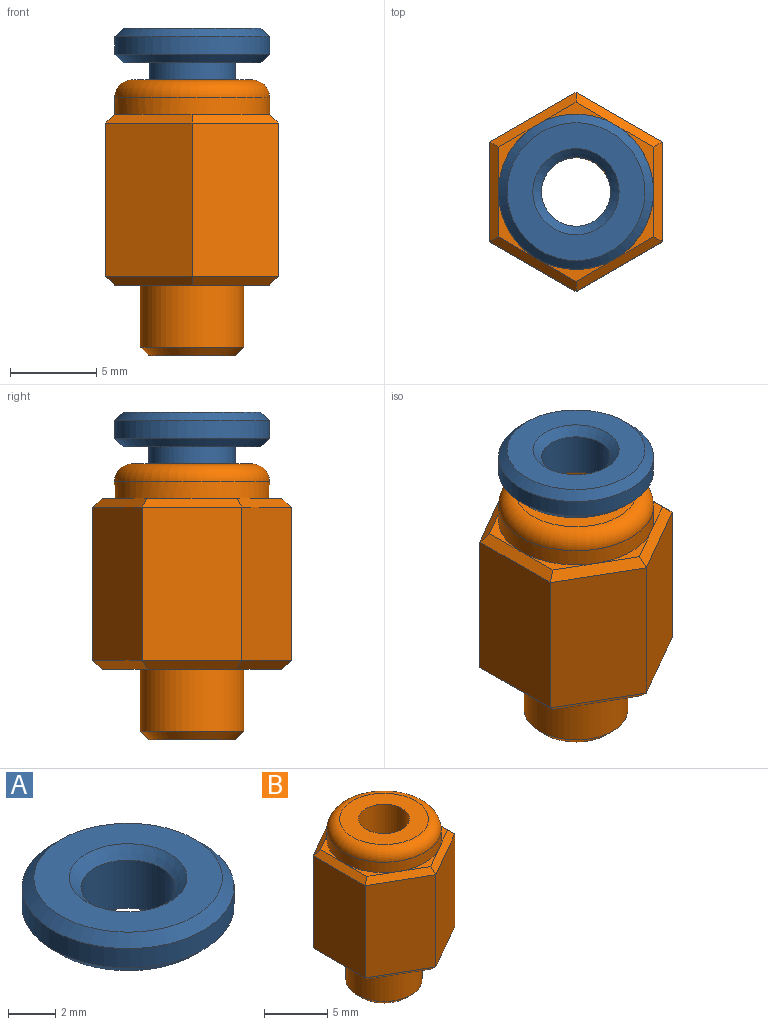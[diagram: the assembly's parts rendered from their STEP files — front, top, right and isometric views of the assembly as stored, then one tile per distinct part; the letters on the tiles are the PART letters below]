
ASSEMBLY  parts=2 mates=1
PART A: 9 faces, bbox 9x9x3 mm
  f0: cylinder r=2.5mm len=5mm, axis (0,0,-1), area 15.7mm2, adj f1,f4
  f1: plane 5x5mm, normal (0,0,-1), area 7.1mm2, adj f0,f5
  f2: cylinder r=4.5mm len=9mm, axis (0,0,-1), area 28.3mm2, adj f6,f8
  f3: plane 8x8mm, normal (0,0,1), area 30.6mm2, adj f7,f8
  f4: plane 8x8mm, normal (0,0,-1), area 30.6mm2, adj f0,f6
  f5: cylinder r=2mm len=4mm, axis (0,0,1), area 31.4mm2, adj f1,f7
  f6: cone r=4.5mm half-angle=45deg, axis (0,0,1), area 18.9mm2, adj f2,f4
  f7: cone r=2mm half-angle=45deg, axis (0,0,1), area 10mm2, adj f3,f5
  f8: cone r=4mm half-angle=45deg, axis (0,0,-1), area 18.9mm2, adj f2,f3
PART B: 32 faces, bbox 10x11.5x16 mm
  f0: plane 3.9x2.25mm, normal (0,0,1), area 1.1mm2, adj f14,f30,f31
  f1: plane 3.9x2.25mm, normal (0,0,1), area 1.1mm2, adj f14,f29,f31
  f2: plane 4.5x1.3mm, normal (0,0,1), area 1.1mm2, adj f14,f27,f29
  f3: plane 3.9x2.25mm, normal (0,0,1), area 1.1mm2, adj f14,f26,f27
  f4: plane 3.9x2.25mm, normal (0,0,1), area 1.1mm2, adj f14,f26,f28
  f5: cylinder r=3mm len=6mm, axis (0,0,1), area 67.9mm2, adj f13,f18
  f6: plane 8.9x5.77mm, normal (-1,0,0), area 51.4mm2, adj f7,f11,f24,f31
  f7: plane 8.9x5mm, normal (-0.5,-0.87,0), area 51.4mm2, adj f6,f8,f25,f29
  f8: plane 8.9x5mm, normal (0.5,-0.87,0), area 51.4mm2, adj f7,f9,f23,f27
  f9: plane 8.9x5.77mm, normal (1,0,0), area 51.4mm2, adj f8,f10,f21,f26
  f10: plane 8.9x5mm, normal (0.5,0.87,0), area 51.4mm2, adj f9,f11,f20,f28
  f11: plane 8.9x5mm, normal (-0.5,0.87,0), area 51.4mm2, adj f6,f10,f22,f30
  f12: plane 4.5x1.3mm, normal (0,0,1), area 1.1mm2, adj f14,f28,f30
  f13: plane 10.39x9mm, normal (0,0,-1), area 41.9mm2, adj f5,f20,f21,f22,f23,f24,f25
  f14: cylinder r=4.5mm len=9mm, axis (0,0,-1), area 28.3mm2, adj f0,f1,f2,f3,f4,f12,f17
  f15: plane 7x7mm, normal (0,0,1), area 25.9mm2, adj f16,f17
  f16: cylinder r=2mm len=15.5mm, axis (0,0,1), area 194.8mm2, adj f15,f19
  f17: torus R=3.5mm, axis (0,0,1), area 40.8mm2, adj f14,f15
  f18: cone r=3mm half-angle=45deg, axis (0,0,1), area 12.2mm2, adj f5,f19
  f19: cone r=2.5mm half-angle=45deg, axis (0,0,-1), area 10mm2, adj f16,f18
  f20: plane 5x3.18mm, normal (0.35,0.61,-0.71), area 3.9mm2, adj f10,f13,f21,f22
  f21: plane 5.77x0.5mm, normal (0.71,0,-0.71), area 3.9mm2, adj f9,f13,f20,f23
  f22: plane 5x3.18mm, normal (-0.35,0.61,-0.71), area 3.9mm2, adj f11,f13,f20,f24
  f23: plane 5x3.18mm, normal (0.35,-0.61,-0.71), area 3.9mm2, adj f8,f13,f21,f25
  f24: plane 5.77x0.5mm, normal (-0.71,0,-0.71), area 3.9mm2, adj f6,f13,f22,f25
  f25: plane 5x3.18mm, normal (-0.35,-0.61,-0.71), area 3.9mm2, adj f7,f13,f23,f24
  f26: plane 5.77x0.5mm, normal (0.71,0,0.71), area 3.9mm2, adj f3,f4,f9,f27,f28
  f27: plane 5x3.18mm, normal (0.35,-0.61,0.71), area 3.9mm2, adj f2,f3,f8,f26,f29
  f28: plane 5x3.18mm, normal (0.35,0.61,0.71), area 3.9mm2, adj f4,f10,f12,f26,f30
  f29: plane 5x3.18mm, normal (-0.35,-0.61,0.71), area 3.9mm2, adj f1,f2,f7,f27,f31
  f30: plane 5x3.18mm, normal (-0.35,0.61,0.71), area 3.9mm2, adj f0,f11,f12,f28,f31
  f31: plane 5.77x0.5mm, normal (-0.71,0,0.71), area 3.9mm2, adj f0,f1,f6,f29,f30
PLACE A at identity
PLACE B at identity fixed
MATE fastened A.f0 <-> B.f5  axis (0,0,-1) through (21.65,-12.5,11.9)mm
